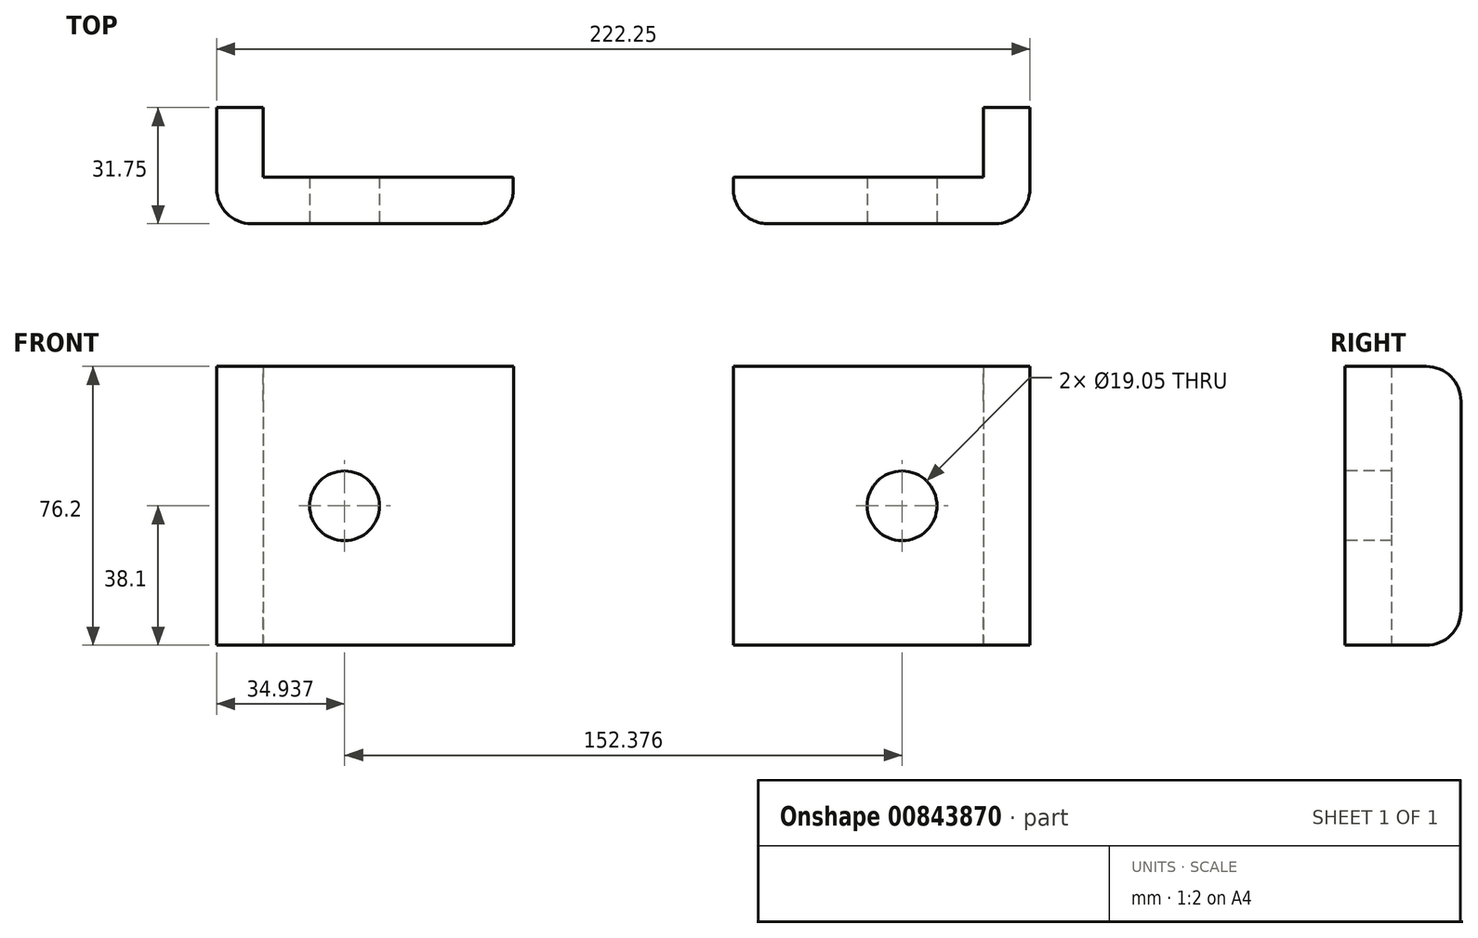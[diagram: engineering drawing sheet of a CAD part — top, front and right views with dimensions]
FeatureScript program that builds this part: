
annotation { "Feature Type Name" : "Feature", "Feature Type Description" : "" }
export const myFeature = defineFeature(function(context is Context, id is Id, definition is map)
    precondition{}
    {
        {
            var Q0;
            Q0=qCreatedBy(makeId("Top.planeOp"),FACE);
            var sketch = newSketch(context, id + "F0", { "sketchPlane" : qUnion([Q0])});
            skLineSegment(sketch, "E0", {"start": v(0, 0) * mm, "end": v(-12.7, 0) * mm});
            skLineSegment(sketch, "E1", {"start": v(-209.55, 0) * mm, "end": v(-222.25, 0) * mm});
            skLineSegment(sketch, "E2", {"start": v(-222.25, 0) * mm, "end": v(-222.25, -31.75) * mm});
            skLineSegment(sketch, "E3", {"start": v(-209.55, 0) * mm, "end": v(-209.55, -19.05) * mm});
            skLineSegment(sketch, "E4", {"start": v(-12.7, 0) * mm, "end": v(-12.7, -19.05) * mm});
            skLineSegment(sketch, "E5", {"start": v(0, 0) * mm, "end": v(0, -31.75) * mm});
            skLineSegment(sketch, "E6", {"start": v(-209.55, -19.05) * mm, "end": v(-12.7, -19.05) * mm});
            skLineSegment(sketch, "E7", {"start": v(-222.25, -31.75) * mm, "end": v(0, -31.75) * mm});
            skCircle(sketch, "E8", {"center": v(-111.12, -19.05) * mm, "radius": 17.46 * mm});
            skCircle(sketch, "E9", {"center": v(-111.12, -19.05) * mm, "radius": 30.16 * mm});
            skSolve(sketch);
        }
        {
            var Q0;
            Q0=makeQuery(id+"F0.imprint","IMPRINT",FACE,{"disambiguationData":[TD([[makeQuery(id+"F0.imprint","IMPRINT",EDGE,{"derivedFrom":sQuery(id+"F0.wireOp",EDGE,"E0")}),1.0]])]});
            var Q1;
            Q1=makeQuery(id+"F0.imprint","IMPRINT",FACE,{"disambiguationData":[TD([[makeQuery(id+"F0.imprint","IMPRINT",EDGE,{"derivedFrom":sQuery(id+"F0.wireOp",EDGE,"E1")}),1.0]])]});
            var Q2;
            {var subQ0=sQuery(id+"F0.wireOp",EDGE,"E9");var subQ1=sQuery(id+"F0.wireOp",EDGE,"E7");var subQ2=makeQuery(id+"F0.imprint","INTERSECT",VERTEX,{"disambiguationData":[OD(0.0)],"derivedFrom":[subQ1,subQ0]});Q2=makeQuery(id+"F0.imprint","IMPRINT",FACE,{"disambiguationData":[TD([[makeQuery(id+"F0.imprint","IMPRINT",EDGE,{"disambiguationData":[TD([[subQ2,-1.0]])],"derivedFrom":subQ1}),-1.0]])]});}
            var Q3;
            {var subQ0=sQuery(id+"F0.wireOp",EDGE,"E9");var subQ1=sQuery(id+"F0.wireOp",EDGE,"E6");var subQ2=makeQuery(id+"F0.imprint","INTERSECT",VERTEX,{"disambiguationData":[OD(0.0)],"derivedFrom":[subQ1,subQ0]});Q3=makeQuery(id+"F0.imprint","IMPRINT",FACE,{"disambiguationData":[TD([[makeQuery(id+"F0.imprint","IMPRINT",EDGE,{"disambiguationData":[TD([[subQ2,-1.0]])],"derivedFrom":subQ1}),-1.0]])]});}
            var Q4;
            {var subQ0=sQuery(id+"F0.wireOp",EDGE,"E9");var subQ1=sQuery(id+"F0.wireOp",EDGE,"E6");var subQ2=makeQuery(id+"F0.imprint","INTERSECT",VERTEX,{"disambiguationData":[OD(1.0)],"derivedFrom":[subQ1,subQ0]});Q4=makeQuery(id+"F0.imprint","IMPRINT",FACE,{"disambiguationData":[TD([[makeQuery(id+"F0.imprint","IMPRINT",EDGE,{"disambiguationData":[TD([[subQ2,1.0]])],"derivedFrom":subQ1}),-1.0]])]});}
            extrude(context, id + "F1", {"entities" : qUnion([Q0, Q1, Q2, Q3, Q4]), "depth" : 76.2 * mm, "offsetDistance" : 25.4 * mm});
        }
        {
            var Q0;
            Q0=makeQuery(id+"F1.opExtrude","CAP_EDGE",EDGE,{"disambiguationData":[OSD([sQuery(id+"F0.wireOp",EDGE,"E0")])],"isStart":true});
            var Q1;
            Q1=makeQuery(id+"F1.opExtrude","CAP_EDGE",EDGE,{"disambiguationData":[OSD([sQuery(id+"F0.wireOp",EDGE,"E0")])],"isStart":false});
            var Q2;
            Q2=makeQuery(id+"F1.opExtrude","CAP_EDGE",EDGE,{"disambiguationData":[OSD([sQuery(id+"F0.wireOp",EDGE,"E1")])],"isStart":false});
            var Q3;
            Q3=makeQuery(id+"F1.opExtrude","CAP_EDGE",EDGE,{"disambiguationData":[OSD([sQuery(id+"F0.wireOp",EDGE,"E1")])],"isStart":true});
            var Q4;
            Q4=makeQuery(id+"F1.opExtrude","SWEPT_EDGE",EDGE,{"disambiguationData":[OSD([sQuery(id+"F0.wireOp",EDGE,"E5"),sQuery(id+"F0.wireOp",EDGE,"E7")])]});
            var Q5;
            Q5=makeQuery(id+"F1.opExtrude","SWEPT_EDGE",EDGE,{"disambiguationData":[OSD([sQuery(id+"F0.wireOp",EDGE,"E2"),sQuery(id+"F0.wireOp",EDGE,"E7")])]});
            var Q6;
            {var subQ0=sQuery(id+"F0.wireOp",EDGE,"E9");var subQ1=sQuery(id+"F0.wireOp",EDGE,"E7");Q6=makeQuery(id+"F1.opExtrude","SWEPT_EDGE",EDGE,{"disambiguationData":[OSD([subQ1,subQ0]),TDD([makeQuery(id+"F0.imprint","INTERSECT",VERTEX,{"disambiguationData":[OD(1.0)],"derivedFrom":[subQ1,subQ0]})])]});}
            var Q7;
            {var subQ0=sQuery(id+"F0.wireOp",EDGE,"E9");var subQ1=sQuery(id+"F0.wireOp",EDGE,"E7");Q7=makeQuery(id+"F1.opExtrude","SWEPT_EDGE",EDGE,{"disambiguationData":[OSD([subQ1,subQ0]),TDD([makeQuery(id+"F0.imprint","INTERSECT",VERTEX,{"disambiguationData":[OD(0.0)],"derivedFrom":[subQ1,subQ0]})])]});}
            fillet(context, id + "F2", {"entities" : qUnion([Q0, Q1, Q2, Q3, Q4, Q5, Q6, Q7]), "radius" : 9.52 * mm, "tangentPropagation" : true, "allowEdgeOverflow" : false});
        }
        {
            var Q0;
            {var subQ0=sQuery(id+"F0.wireOp",EDGE,"E7");Q0=makeQuery(id+"F1.opExtrude","SWEPT_FACE",FACE,{"disambiguationData":[OSD([subQ0]),TDD([makeQuery(id+"F0.imprint","IMPRINT",EDGE,{"disambiguationData":[TD([[makeQuery(id+"F0.imprint","INTERSECT",VERTEX,{"derivedFrom":[sQuery(id+"F0.wireOp",EDGE,"E2"),subQ0]}),-1.0]])],"derivedFrom":subQ0})])]});}
            var sketch = newSketch(context, id + "F3", { "sketchPlane" : qUnion([Q0])});
            skLineSegment(sketch, "E10", {"start": v(-144, 76.2) * mm, "end": v(-187.31, 76.2) * mm});
            skLineSegment(sketch, "E11", {"start": v(-187.31, 76.2) * mm, "end": v(-187.31, 38.1) * mm});
            skLineSegment(sketch, "E12", {"start": v(-187.31, 38.1) * mm, "end": v(-187.31, 0) * mm});
            skCircle(sketch, "E13", {"center": v(-187.31, 38.1) * mm, "radius": 9.53 * mm});
            skSolve(sketch);
        }
        {
            var Q0;
            {var subQ0=sQuery(id+"F0.wireOp",EDGE,"E7");Q0=makeQuery(id+"F1.opExtrude","SWEPT_FACE",FACE,{"disambiguationData":[OSD([subQ0]),TDD([makeQuery(id+"F0.imprint","IMPRINT",EDGE,{"disambiguationData":[TD([[makeQuery(id+"F0.imprint","INTERSECT",VERTEX,{"derivedFrom":[sQuery(id+"F0.wireOp",EDGE,"E5"),subQ0]}),1.0]])],"derivedFrom":subQ0})])]});}
            var sketch = newSketch(context, id + "F4", { "sketchPlane" : qUnion([Q0])});
            skLineSegment(sketch, "E14", {"start": v(-78.24, 76.2) * mm, "end": v(-34.94, 76.2) * mm});
            skLineSegment(sketch, "E15", {"start": v(-34.94, 76.2) * mm, "end": v(-34.94, 38.1) * mm});
            skLineSegment(sketch, "E16", {"start": v(-34.94, 38.1) * mm, "end": v(-34.94, 0) * mm});
            skCircle(sketch, "E17", {"center": v(-34.94, 38.1) * mm, "radius": 9.53 * mm});
            skSolve(sketch);
        }
        {
            var Q0;
            Q0 = qSketchRegion(id + "F4", true);
            var Q1;
            {var subQ0=sQuery(id+"F3.wireOp",EDGE,"E12");var subQ1=sQuery(id+"F3.wireOp",EDGE,"E11");var subQ2=makeQuery(id+"F3.imprint","INTERSECT",VERTEX,{"derivedFrom":[subQ1,subQ0]});Q1=makeQuery(id+"F3.imprint","IMPRINT",FACE,{"disambiguationData":[TD([[makeQuery(id+"F3.imprint","IMPRINT",EDGE,{"disambiguationData":[TD([[subQ2,1.0]])],"derivedFrom":subQ1}),1.0]])]});}
            var Q2;
            {var subQ0=sQuery(id+"F3.wireOp",EDGE,"E12");var subQ1=sQuery(id+"F3.wireOp",EDGE,"E11");var subQ2=makeQuery(id+"F3.imprint","INTERSECT",VERTEX,{"derivedFrom":[subQ1,subQ0]});Q2=makeQuery(id+"F3.imprint","IMPRINT",FACE,{"disambiguationData":[TD([[makeQuery(id+"F3.imprint","IMPRINT",EDGE,{"disambiguationData":[TD([[subQ2,1.0]])],"derivedFrom":subQ1}),-1.0]])]});}
            extrude(context, id + "F5", {"entities" : qUnion([Q0, Q1, Q2]), "operationType" : NewBodyOperationType.REMOVE, "oppositeDirection" : true, "depth" : 25.4 * mm, "offsetDistance" : 25.4 * mm});
        }
    });
